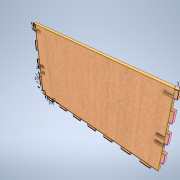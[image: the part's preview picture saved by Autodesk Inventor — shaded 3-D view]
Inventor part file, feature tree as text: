
AUTODESK INVENTOR PART (.ipt)
format: ipt  version: 2021 (Build 250183000, 183)  size: 238,080 bytes
history: native  units: mm
features: extrude x3, sketch x3
ambient origin geometry x8: Origin, YZ Plane, XZ Plane, XY Plane, X Axis, Y Axis, Z Axis, Center Point
bodies: Solid1 (feature_tree)
feature tree (6):
  extrude  "Extrusion1"  Depth=77.0mm
  extrude  "Extrusion2"  Depth=3.0mm
  extrude  "Extrusion3"  Depth=70.0mm
  sketch  "Sketch1"  dims[d0=144.0mm d1=77.0mm]
  sketch  "Sketch2"  dims[d2=3.0mm d3=0.0mm d4=3.0mm]
  sketch  "Sketch3"  dims[d5=10.0mm d6=70.0mm d8=20.0mm d9=10.0mm d11=10.0mm d13=3.0mm d14=10.0mm d15=30.0mm d17=20.0mm d18=10.0mm d20=10.0mm d22=3.0mm d23=7.0mm d24=3.0mm d25=3.0mm d26=0.0mm d27=7.0mm d28=3.0mm d29=20.0mm d31=137.0mm d32=20.0mm d34=37.0mm d37=0.0mm d38=0.0mm d39=20.0mm d41=7.0mm d42=20.0mm d44=137.0mm d47=4.0mm]
